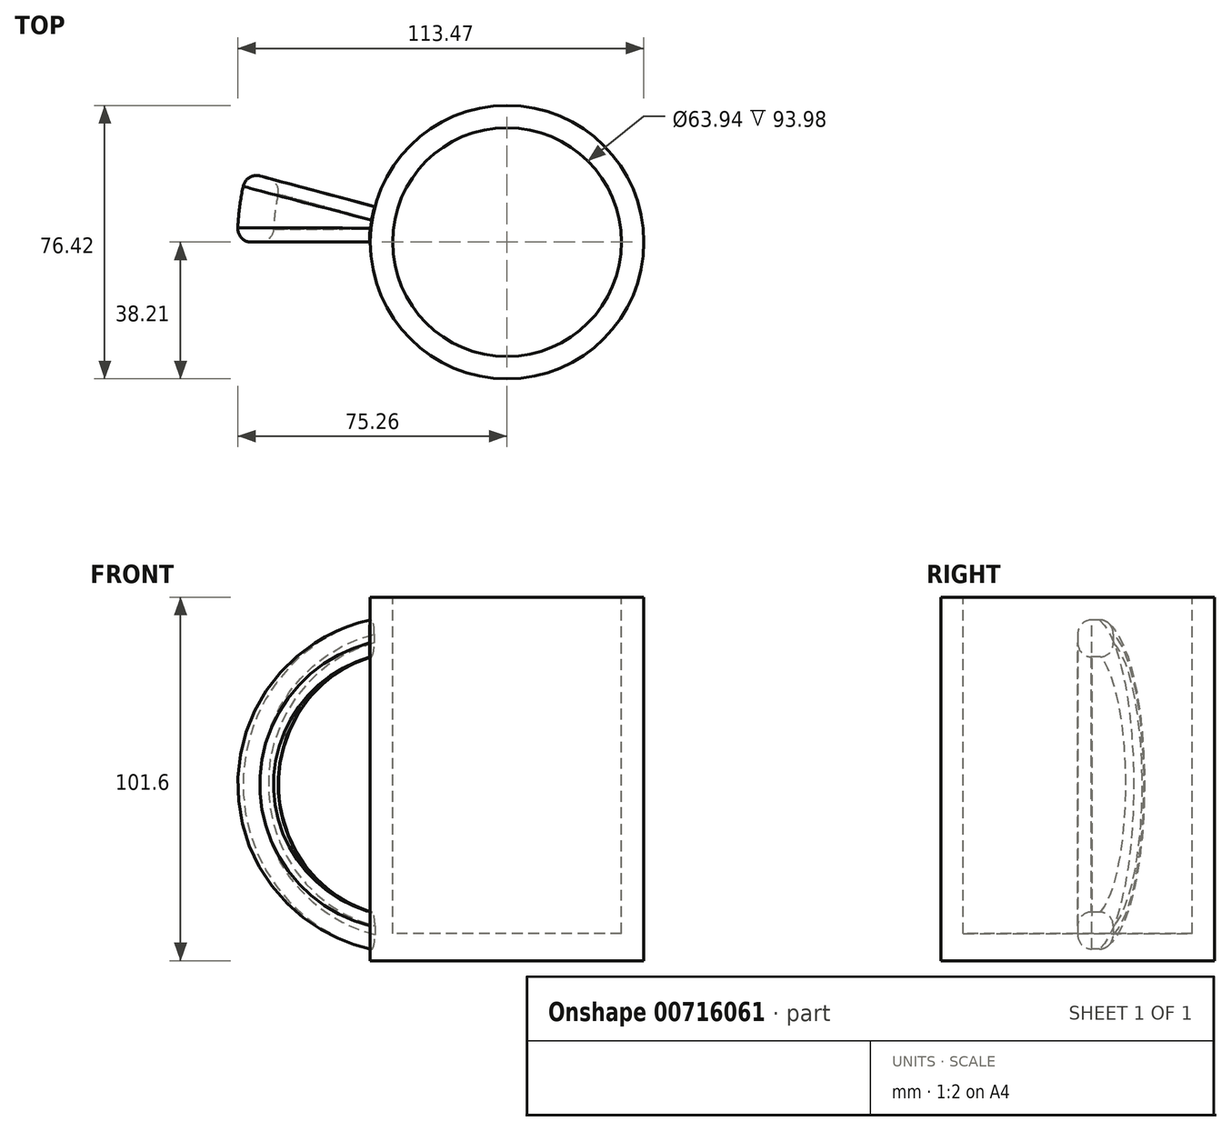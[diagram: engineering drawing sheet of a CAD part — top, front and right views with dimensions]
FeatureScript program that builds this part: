
annotation { "Feature Type Name" : "Feature", "Feature Type Description" : "" }
export const myFeature = defineFeature(function(context is Context, id is Id, definition is map)
    precondition{}
    {
        {
            var Q0;
            Q0=qCreatedBy(makeId("Top.planeOp"),FACE);
            var sketch = newSketch(context, id + "F0", { "sketchPlane" : qUnion([Q0])});
            skCircle(sketch, "E0", {"center": v(0, 0) * mm, "radius": 38.21 * mm});
            skSolve(sketch);
        }
        {
            var Q0;
            Q0 = qSketchRegion(id + "F0", true);
            extrude(context, id + "F1", {"entities" : qUnion([Q0]), "depth" : 101.6 * mm, "offsetDistance" : 25.4 * mm});
        }
        {
            var Q0;
            Q0=makeQuery(id+"F1.opExtrude","CAP_FACE",FACE,{"disambiguationData":[OSD([sQuery(id+"F0.wireOp",EDGE,"E0")])],"isStart":false});
            var sketch = newSketch(context, id + "F2", { "sketchPlane" : qUnion([Q0])});
            skCircle(sketch, "E1", {"center": v(0, 0) * mm, "radius": 31.97 * mm});
            skSolve(sketch);
        }
        {
            var Q0;
            Q0 = qSketchRegion(id + "F2", true);
            extrude(context, id + "F3", {"entities" : qUnion([Q0]), "operationType" : NewBodyOperationType.REMOVE, "oppositeDirection" : true, "depth" : 93.98 * mm, "offsetDistance" : 25.4 * mm});
        }
        {
            var Q0;
            Q0=qCreatedBy(makeId("Front.planeOp"),FACE);
            var sketch = newSketch(context, id + "F4", { "sketchPlane" : qUnion([Q0])});
            skArc(sketch, "E2", {"start": v(-38.44, 84.9) * mm, "mid": v(-65.36, 48.95) * mm, "end": v(-37.82, 13.46) * mm});
            skArc(sketch, "E3", {"start": v(-38.32, 95.24) * mm, "mid": v(-75.36, 49.06) * mm, "end": v(-37.93, 3.2) * mm});
            skLineSegment(sketch, "E4", {"start": v(-37.93, 3.2) * mm, "end": v(-37.82, 13.46) * mm});
            skLineSegment(sketch, "E5", {"start": v(-38.32, 95.24) * mm, "end": v(-38.44, 84.9) * mm});
            skSolve(sketch);
        }
        {
            var Q0;
            Q0=makeQuery(id+"F4.imprint","IMPRINT",FACE,{"disambiguationData":[TD([[makeQuery(id+"F4.imprint","IMPRINT",EDGE,{"derivedFrom":sQuery(id+"F4.wireOp",EDGE,"E2")}),-1.0]])]});
            var Q1;
            Q1=makeQuery(id+"F1.opExtrude","SWEPT_FACE",FACE,{"disambiguationData":[OSD([sQuery(id+"F0.wireOp",EDGE,"E0")])]});
            revolve(context, id + "F5", {"operationType" : NewBodyOperationType.ADD, "surfaceOperationType" : NewSurfaceOperationType.NEW, "entities" : qUnion([Q0]), "axis" : qUnion([Q1]), "revolveType" : RevolveType.ONE_DIRECTION, "angle" : 15 * degree});
        }
        {
            var Q0;
            Q0=makeQuery(id+"F5.opRevolve","CAP_EDGE",EDGE,{"disambiguationData":[OSD([sQuery(id+"F4.wireOp",EDGE,"E2")])],"isStart":false});
            var Q1;
            Q1=makeQuery(id+"F5.opRevolve","CAP_EDGE",EDGE,{"disambiguationData":[OSD([sQuery(id+"F4.wireOp",EDGE,"E3")])],"isStart":false});
            var Q2;
            Q2=makeQuery(id+"F5.opRevolve","CAP_EDGE",EDGE,{"disambiguationData":[OSD([sQuery(id+"F4.wireOp",EDGE,"E2")])],"isStart":true});
            var Q3;
            Q3=makeQuery(id+"F5.opRevolve","CAP_EDGE",EDGE,{"disambiguationData":[OSD([sQuery(id+"F4.wireOp",EDGE,"E3")])],"isStart":true});
            fillet(context, id + "F6", {"entities" : qUnion([Q0, Q1, Q2, Q3]), "radius" : 3.8 * mm, "tangentPropagation" : true, "allowEdgeOverflow" : false});
        }
    });
